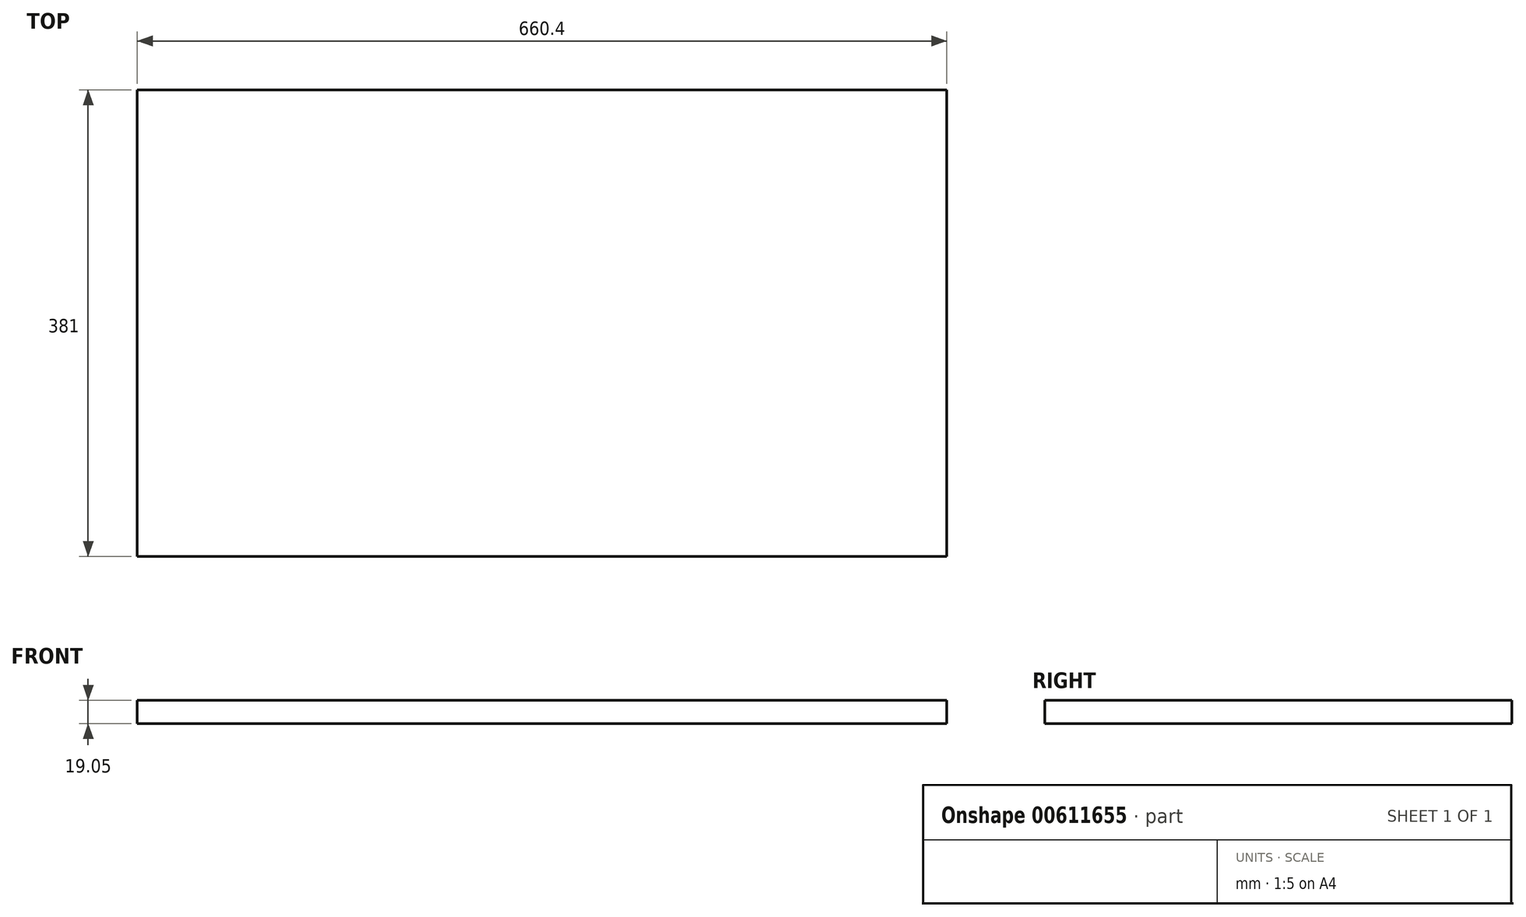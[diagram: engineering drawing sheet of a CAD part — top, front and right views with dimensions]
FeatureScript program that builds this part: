
annotation { "Feature Type Name" : "Feature", "Feature Type Description" : "" }
export const myFeature = defineFeature(function(context is Context, id is Id, definition is map)
    precondition{}
    {
        {
            var Q0;
            Q0=qCreatedBy(makeId("Top.planeOp"),FACE);
            var sketch = newSketch(context, id + "F0", { "sketchPlane" : qUnion([Q0])});
            skLineSegment(sketch, "E0", {"start": v(-316.53, 112.68) * mm, "end": v(343.87, 112.68) * mm});
            skLineSegment(sketch, "E1", {"start": v(343.87, 112.68) * mm, "end": v(343.87, -268.32) * mm});
            skLineSegment(sketch, "E2", {"start": v(343.87, -268.32) * mm, "end": v(-316.53, -268.32) * mm});
            skLineSegment(sketch, "E3", {"start": v(-316.53, -268.32) * mm, "end": v(-316.53, 112.68) * mm});
            skSolve(sketch);
        }
        {
            var Q0;
            Q0=makeQuery(id+"F0.imprint","IMPRINT",FACE,{"disambiguationData":[TD([[makeQuery(id+"F0.imprint","IMPRINT",EDGE,{"derivedFrom":sQuery(id+"F0.wireOp",EDGE,"E0")}),-1.0]])]});
            extrude(context, id + "F1", {"entities" : qUnion([Q0]), "depth" : 19.05 * mm, "offsetDistance" : 25.4 * mm});
        }
    });
